# Revit family: Fixed
name_source: partatom
category: Windows
revit_build: Autodesk Revit 2017 (Build: 20161006_0315(x64)
units: mm (PartAtom-declared; Revit-internal decimal feet)

## family parameters
Always vertical = Yes
Cut with Voids When Loaded = No
Host = Wall
Room Calculation Point = No
Shared = No

## types (1)
- Fixed
    Analytic Construction = <None>
    Area = 1.41 m²
    Case Depth = 115 mm  [stored 0.377297 ft]
    Case Width = 45 mm
    Case/Transom = <By Category>
    Default Sill Height = 800 mm
    Embrasure = <By Category>
    Glass = <By Category>
    Glass Area = 1.21 m²
    Glass Thickness = 28 mm
    Height = 1188 mm
    Rebate Depth = 50 mm
    Rough Area = 1.47 m²
    Rough Height = 1212 mm  [stored 3.97638 ft]
    Rough Width = 1212 mm  [stored 3.97638 ft]
    Seal Width = 12 mm  [stored 0.0393701 ft]
    Sealing = No
    Sill Plate = <By Category>
    Wall Closure = Neither
    Wall Surface = <By Category>
    Width = 1188 mm
    length#1 = 0 mm  [stored 0 ft]
    length#2 = 57 mm  [stored 0.187008 ft]
    length#3 = 100 mm  [stored 0.328084 ft]
    length#4 = -50 mm  [stored -0.164042 ft]
    length#5 = -22 mm  [stored -0.0721785 ft]

note: [stored X ft] marks values corroborated as IEEE doubles in the binary element streams (Revit-internal decimal feet)

## geometry (parser evidence)
native form markers: Sweep x5
no freeform markers — native parametric forms only
